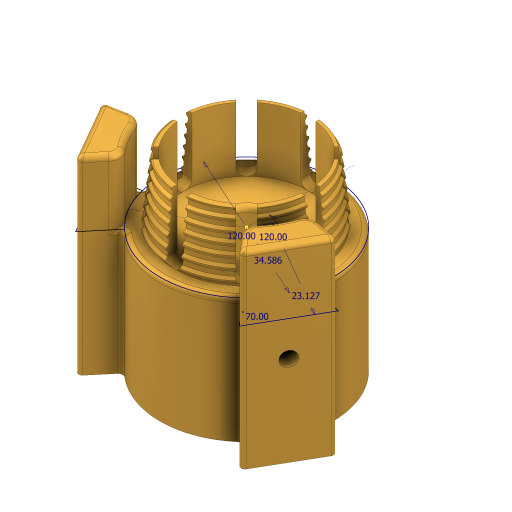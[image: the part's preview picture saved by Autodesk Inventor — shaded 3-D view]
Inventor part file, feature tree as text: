
AUTODESK INVENTOR PART (.ipt)
format: ipt  version: 2023 (Build 270158000, 158)  size: 3,035,136 bytes
history: native  units: mm
features: sketch x9, fillet x8, extrude x7, hole x3, draft x2, helix x2, direct_edit x1, pattern_circular x1, chamfer x1, other x1
ambient origin geometry x8: Origin, YZ Plane, XZ Plane, XY Plane, X Axis, Y Axis, Z Axis, Center Point
bodies: Solid1 (feature_tree)
feature tree (35):
  extrude  "Extrusion1"  Depth=26.5mm
  draft  "FaceDraft1"
  sketch  "Sketch2"  dims[d34=0.0mm d35=0.0mm d56=8.726646mm]
  helix  "Coil3"  [1 undecoded]
  helix  "Coil4"  [1 undecoded]
  direct_edit  "Direct Edit2"
  extrude  "Extrusion2"  Depth=8.726646mm
  extrude  "Extrusion13"  TaperAngle=90.0deg  [1 undecoded]
  extrude  "Extrusion14"  Depth=34.58632mm
  extrude  "Extrusion15"  TaperAngle=120.0deg  [1 undecoded]
  fillet  "Fillet10"  Radius=23.127mm
  extrude  "Extrusion16"  Depth=25.0mm TaperAngle=0.0deg
  pattern_circular  "Circular Pattern3"  Count=8 Angle=360.0deg
  hole  "Hole3"  [1 undecoded]
  hole  "Hole4"  [1 undecoded]
  fillet  "Fillet11"  Radius=1.5mm
  fillet  "Fillet12"  Radius=12.0mm
  fillet  "Fillet13"  Radius=2.5mm
  extrude  "Extrusion18"  Depth=1.0mm
  draft  "FaceDraft6"
  chamfer  "Chamfer3"  Distance=7.0mm
  fillet  "Fillet16"  Radius=10.0mm
  hole  "Hole6"  [1 undecoded]
  fillet  "Fillet17"  Radius=5.0mm
  fillet  "Fillet18"  [1 undecoded]
  fillet  "Fillet19"  Radius=2.0mm
  sketch  "Sketch1"  dims[d0=25.0mm d1=26.5mm d2=12.875mm d3=0.0mm d4=1.047198mm]
  sketch  "Sketch3"  dims[d62=2.0mm d63=13.0mm d64=10.0mm d65=1.047198mm]
  sketch  "Sketch11"  dims[d66=90.0deg d67=90.0deg d68=0.0mm d69=0.0mm d70=2.0mm d71=3.0mm d72=10.0mm d73=-1.047198mm d74=90.0deg d75=90.0deg d76=0.0mm d77=0.0mm]
  sketch  "Sketch13"  dims[d79=-0.127mm d145=34.58632mm]
  sketch  "Sketch14"  dims[d150=120.0deg d151=120.0deg d153=23.127mm]
  sketch  "Sketch16"  dims[d154=12.217305mm d157=25.0mm d158=0.0mm]
  sketch  "Sketch19"  dims[d159=3.0mm d160=80.0mm d162=360.0deg]
  sketch  "Sketch20"  dims[d164=0.0mm d165=0.0mm d166=1.0mm d179=5.3mm d180=6.0mm d181=4.0mm d182=2.0mm d183=90.0deg d184=5.0mm d185=0.0mm d186=10.0mm d187=6.0mm d188=4.0mm d189=2.0mm d190=90.0deg d191=15.0mm d192=0.0mm d193=1.0mm d194=1.5mm d195=12.0mm d196=0.0mm d197=2.5mm d208=2.9mm d209=7.0mm d210=10.0mm d211=0.0mm d212=20.0mm d213=120.0deg d223=6.0mm d224=7.0mm d225=0.0mm d226=0.0mm d227=10.0mm d228=5.0mm d229=0.0mm d230=-4.363323mm d231=0.33mm d232=2.0mm d233=45.0deg d234=0.75mm d235=5.3mm d236=6.0mm d237=20.0mm d238=2.0mm d239=90.0deg d240=10.0mm d241=0.0mm d242=0.75mm d243=1.0mm d244=1.0mm d109=0.5mm d110=0.872665mm d111=0.5mm d112=0.872665mm d245=0.0mm]
  other  "Size2"
note: 8 required parameter values undecoded (feature->parameter linkage not recoverable at this tier; creation-order binding heuristic only, values carry confidence <= 0.55)
